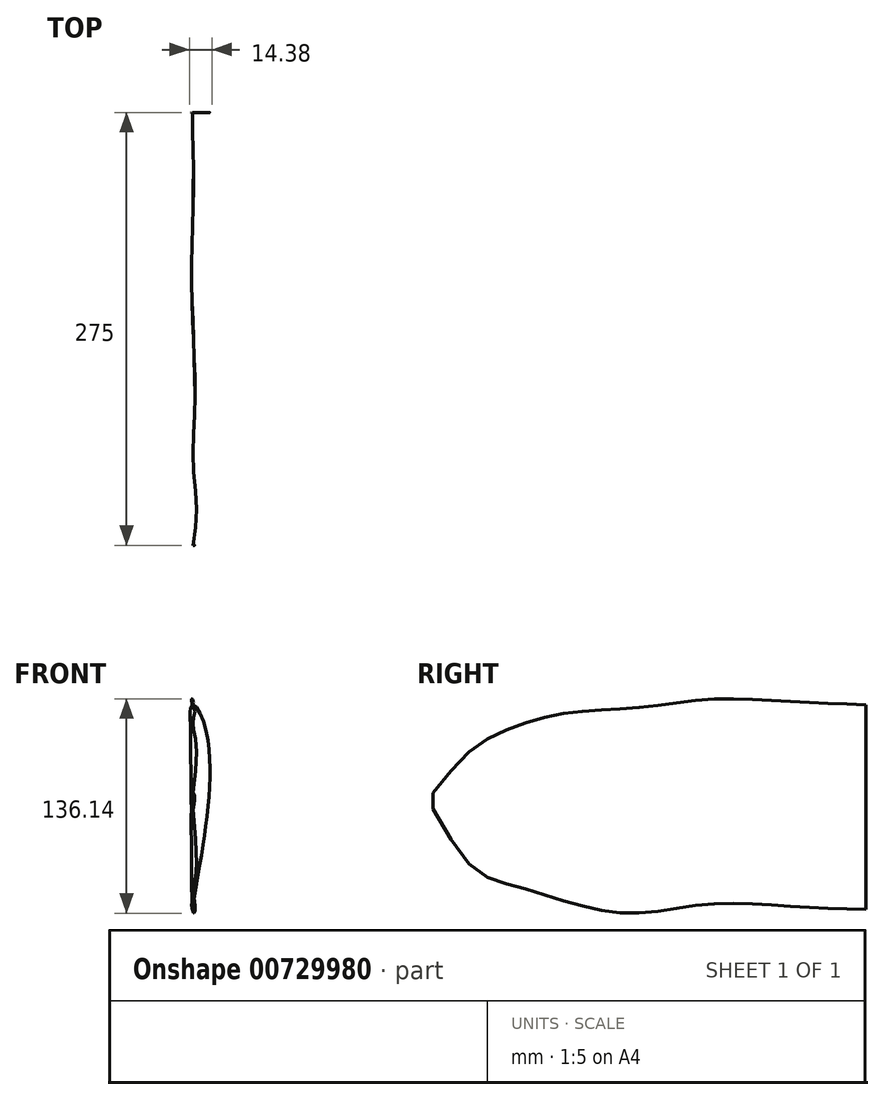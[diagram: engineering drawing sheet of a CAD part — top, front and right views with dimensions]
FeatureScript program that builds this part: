
annotation { "Feature Type Name" : "Feature", "Feature Type Description" : "" }
export const myFeature = defineFeature(function(context is Context, id is Id, definition is map)
    precondition{}
    {
        {
            var Q0;
            Q0=qCreatedBy(makeId("Front.planeOp"),FACE);
            var sketch = newSketch(context, id + "F0", { "sketchPlane" : qUnion([Q0])});
            skFitSpline(sketch, "E0", {"points": [v(-0.6, 60.6) * mm, v(1, 59.9) * mm, v(2.6, 58.2) * mm, v(5, 54) * mm, v(7.3, 47.68) * mm, v(9.21, 39.37) * mm, v(10.11, 32.86) * mm, v(10.51, 25.45) * mm, v(10.61, 18.53) * mm, v(10.51, 11.72) * mm, v(10.11, 3.4) * mm, v(9.51, -3.7) * mm, v(8.4, -12.72) * mm, v(7.5, -20.14) * mm, v(6.55, -27.22) * mm, v(5, -36.27) * mm, v(3.57, -44.14) * mm, v(2.38, -51.16) * mm, v(1.31, -58.43) * mm, v(0.24, -64.75) * mm, v(-0.6, -69.4) * mm], "startDerivative": vector(64.1, -21.66) * mm, "endDerivative": vector(-18.95, -105.25) * mm});
            skFitSpline(sketch, "E1", {"points": [v(-0.6, 60.6) * mm, v(-1.58, 60.1) * mm, v(-1.78, 59.05) * mm, v(-1.93, 58.05) * mm, v(-1.93, 55.8) * mm, v(-1.93, 52.8) * mm, v(-1.83, 48.73) * mm, v(-1.73, 46.83) * mm, v(-1.73, 43.73) * mm, v(-1.73, 40.17) * mm, v(-1.73, 37.41) * mm, v(-1.59, 31.92) * mm, v(-1.59, 28) * mm, v(-1.53, 20.9) * mm, v(-1.47, 11.61) * mm, v(-1.47, 4.1) * mm, v(-1.26, -4.02) * mm, v(-1.26, -8.06) * mm, v(-1.26, -17.16) * mm, v(-1.18, -30.26) * mm, v(-1.16, -34.22) * mm, v(-0.97, -44.95) * mm, v(-0.93, -58.54) * mm, v(-0.6, -69.4) * mm], "startDerivative": vector(-58.23, -16.82) * mm, "endDerivative": vector(6.63, -165.01) * mm});
            skSolve(sketch);
        }
        {
            var Q0;
            Q0=qCreatedBy(makeId("Front.planeOp"),FACE);
            cPlane(context, id + "F1", {"entities" : qUnion([Q0]), "cplaneType" : CPlaneType.OFFSET, "offset" : 275 * mm, "width" : 150 * mm, "height" : 150 * mm});
        }
        {
            var Q0;
            Q0=qCreatedBy(id+"F1.planeOp",FACE);
            var sketch = newSketch(context, id + "F2", { "sketchPlane" : qUnion([Q0])});
            skFitSpline(sketch, "E2", {"points": [v(0, 4.66) * mm, v(0.12, 4.6) * mm, v(0.25, 4.47) * mm, v(0.43, 4.15) * mm, v(0.6, 3.66) * mm, v(0.75, 3.02) * mm, v(0.82, 2.52) * mm, v(0.85, 1.95) * mm, v(0.86, 1.42) * mm, v(0.85, 0.9) * mm, v(0.82, 0.26) * mm, v(0.78, -0.3) * mm, v(0.7, -0.98) * mm, v(0.62, -1.55) * mm, v(0.55, -2.1) * mm, v(0.43, -2.8) * mm, v(0.32, -3.4) * mm, v(0.23, -3.94) * mm, v(0.15, -4.5) * mm, v(0.06, -4.99) * mm, v(0, -5.34) * mm], "startDerivative": vector(4.93, -1.67) * mm, "endDerivative": vector(-1.46, -8.1) * mm});
            skFitSpline(sketch, "E3", {"points": [v(0, 4.66) * mm, v(-0.08, 4.62) * mm, v(-0.1, 4.54) * mm, v(-0.1, 4.46) * mm, v(-0.1, 4.29) * mm, v(-0.1, 4.06) * mm, v(-0.1, 3.74) * mm, v(-0.09, 3.6) * mm, v(-0.09, 3.36) * mm, v(-0.09, 3.08) * mm, v(-0.09, 2.87) * mm, v(-0.08, 2.45) * mm, v(-0.08, 2.15) * mm, v(-0.07, 1.6) * mm, v(-0.07, 0.89) * mm, v(-0.07, 0.31) * mm, v(-0.05, -0.31) * mm, v(-0.05, -0.63) * mm, v(-0.05, -1.33) * mm, v(-0.04, -2.33) * mm, v(-0.04, -2.64) * mm, v(-0.03, -3.46) * mm, v(-0.03, -4.5) * mm, v(0, -5.34) * mm], "startDerivative": vector(-4.48, -1.3) * mm, "endDerivative": vector(0.5, -12.7) * mm});
            skSolve(sketch);
        }
        {
            var Q0;
            Q0=qCreatedBy(makeId("Front.planeOp"),FACE);
            cPlane(context, id + "F3", {"entities" : qUnion([Q0]), "cplaneType" : CPlaneType.OFFSET, "offset" : 250 * mm, "width" : 150 * mm, "height" : 150 * mm});
        }
        {
            var Q0;
            Q0=qCreatedBy(id+"F3.planeOp",FACE);
            var sketch = newSketch(context, id + "F4", { "sketchPlane" : qUnion([Q0])});
            skFitSpline(sketch, "E4", {"points": [v(2.07, 32.54) * mm, v(3, 32.13) * mm, v(3.92, 31.15) * mm, v(5.3, 28.72) * mm, v(6.64, 25.08) * mm, v(7.73, 20.29) * mm, v(8.25, 16.53) * mm, v(8.49, 12.25) * mm, v(8.54, 8.27) * mm, v(8.49, 4.34) * mm, v(8.25, -0.46) * mm, v(7.9, -4.57) * mm, v(7.27, -9.77) * mm, v(6.75, -14.04) * mm, v(6.2, -18.13) * mm, v(5.3, -23.35) * mm, v(4.48, -27.9) * mm, v(3.8, -31.95) * mm, v(3.18, -36.14) * mm, v(2.56, -39.78) * mm, v(2.08, -42.46) * mm], "startDerivative": vector(36.99, -12.5) * mm, "endDerivative": vector(-10.93, -60.72) * mm});
            skFitSpline(sketch, "E5", {"points": [v(2.07, 32.54) * mm, v(1.5, 32.25) * mm, v(1.4, 31.64) * mm, v(1.3, 31.06) * mm, v(1.3, 29.76) * mm, v(1.3, 28.03) * mm, v(1.36, 25.69) * mm, v(1.42, 24.6) * mm, v(1.42, 22.8) * mm, v(1.42, 20.75) * mm, v(1.42, 19.16) * mm, v(1.5, 15.99) * mm, v(1.5, 13.72) * mm, v(1.54, 9.63) * mm, v(1.57, 4.27) * mm, v(1.57, -0.06) * mm, v(1.7, -4.75) * mm, v(1.7, -7.08) * mm, v(1.7, -12.33) * mm, v(1.74, -19.88) * mm, v(1.75, -22.17) * mm, v(1.86, -28.36) * mm, v(1.88, -36.2) * mm, v(2.08, -42.46) * mm], "startDerivative": vector(-33.6, -9.7) * mm, "endDerivative": vector(3.82, -95.2) * mm});
            skSolve(sketch);
        }
        {
            var Q0;
            Q0=qCreatedBy(makeId("Front.planeOp"),FACE);
            cPlane(context, id + "F5", {"entities" : qUnion([Q0]), "cplaneType" : CPlaneType.OFFSET, "offset" : 225 * mm, "width" : 150 * mm, "height" : 150 * mm});
        }
        {
            var Q0;
            Q0=qCreatedBy(id+"F5.planeOp",FACE);
            var sketch = newSketch(context, id + "F6", { "sketchPlane" : qUnion([Q0])});
            skFitSpline(sketch, "E6", {"points": [v(0, 46.1) * mm, v(1.22, 45.55) * mm, v(2.46, 44.24) * mm, v(4.3, 41) * mm, v(6.08, 36.15) * mm, v(7.54, 29.75) * mm, v(8.24, 24.75) * mm, v(8.55, 19.04) * mm, v(8.62, 13.73) * mm, v(8.55, 8.49) * mm, v(8.24, 2.1) * mm, v(7.77, -3.38) * mm, v(6.93, -10.32) * mm, v(6.23, -16.02) * mm, v(5.5, -21.47) * mm, v(4.3, -28.43) * mm, v(3.2, -34.48) * mm, v(2.3, -39.89) * mm, v(1.47, -45.48) * mm, v(0.64, -50.33) * mm, v(0, -53.9) * mm], "startDerivative": vector(49.31, -16.66) * mm, "endDerivative": vector(-14.58, -80.96) * mm});
            skFitSpline(sketch, "E7", {"points": [v(0, 46.1) * mm, v(-0.76, 45.7) * mm, v(-0.91, 44.9) * mm, v(-1.03, 44.13) * mm, v(-1.03, 42.4) * mm, v(-1.03, 40.08) * mm, v(-0.95, 36.96) * mm, v(-0.87, 35.5) * mm, v(-0.87, 33.1) * mm, v(-0.87, 30.37) * mm, v(-0.87, 28.25) * mm, v(-0.76, 24.03) * mm, v(-0.76, 21) * mm, v(-0.72, 15.55) * mm, v(-0.67, 8.4) * mm, v(-0.67, 2.63) * mm, v(-0.51, -3.62) * mm, v(-0.51, -6.73) * mm, v(-0.51, -13.73) * mm, v(-0.45, -23.8) * mm, v(-0.43, -26.85) * mm, v(-0.29, -35.1) * mm, v(-0.26, -45.56) * mm, v(0, -53.9) * mm], "startDerivative": vector(-44.8, -12.94) * mm, "endDerivative": vector(5.1, -126.93) * mm});
            skSolve(sketch);
        }
        {
            var Q0;
            Q0=qCreatedBy(makeId("Front.planeOp"),FACE);
            cPlane(context, id + "F7", {"entities" : qUnion([Q0]), "cplaneType" : CPlaneType.OFFSET, "offset" : 190 * mm, "width" : 150 * mm, "height" : 150 * mm});
        }
        {
            var Q0;
            Q0=qCreatedBy(id+"F7.planeOp",FACE);
            var sketch = newSketch(context, id + "F8", { "sketchPlane" : qUnion([Q0])});
            skFitSpline(sketch, "E8", {"points": [v(0.85, 55.55) * mm, v(2.33, 54.9) * mm, v(3.81, 53.33) * mm, v(6.03, 49.44) * mm, v(8.16, 43.62) * mm, v(9.92, 35.94) * mm, v(10.75, 29.93) * mm, v(11.12, 23.09) * mm, v(11.21, 16.7) * mm, v(11.12, 10.42) * mm, v(10.75, 2.75) * mm, v(10.2, -3.82) * mm, v(9.18, -12.14) * mm, v(8.35, -18.99) * mm, v(7.46, -25.52) * mm, v(6.03, -33.88) * mm, v(4.71, -41.14) * mm, v(3.61, -47.63) * mm, v(2.62, -54.34) * mm, v(1.63, -60.16) * mm, v(0.86, -64.45) * mm], "startDerivative": vector(59.18, -20) * mm, "endDerivative": vector(-17.5, -97.15) * mm});
            skFitSpline(sketch, "E9", {"points": [v(0.85, 55.55) * mm, v(-0.05, 55.08) * mm, v(-0.23, 54.11) * mm, v(-0.37, 53.19) * mm, v(-0.37, 51.1) * mm, v(-0.37, 48.33) * mm, v(-0.28, 44.59) * mm, v(-0.18, 42.83) * mm, v(-0.18, 39.96) * mm, v(-0.18, 36.68) * mm, v(-0.18, 34.14) * mm, v(-0.05, 29.07) * mm, v(-0.05, 25.44) * mm, v(0, 18.9) * mm, v(0.06, 10.32) * mm, v(0.06, 3.4) * mm, v(0.25, -4.1) * mm, v(0.25, -7.84) * mm, v(0.25, -16.24) * mm, v(0.33, -28.33) * mm, v(0.35, -31.99) * mm, v(0.52, -41.9) * mm, v(0.56, -54.44) * mm, v(0.86, -64.45) * mm], "startDerivative": vector(-53.75, -15.52) * mm, "endDerivative": vector(6.12, -152.32) * mm});
            skSolve(sketch);
        }
        {
            var Q0;
            Q0=qCreatedBy(makeId("Front.planeOp"),FACE);
            cPlane(context, id + "F9", {"entities" : qUnion([Q0]), "cplaneType" : CPlaneType.OFFSET, "offset" : 50 * mm, "width" : 150 * mm, "height" : 150 * mm});
        }
        {
            var Q0;
            Q0=qCreatedBy(id+"F9.planeOp",FACE);
            var sketch = newSketch(context, id + "F10", { "sketchPlane" : qUnion([Q0])});
            skFitSpline(sketch, "E10", {"points": [v(-0.01, 62.92) * mm, v(1.6, 62.22) * mm, v(3.2, 60.52) * mm, v(5.6, 56.3) * mm, v(7.9, 50) * mm, v(9.8, 41.68) * mm, v(10.7, 35.17) * mm, v(11.1, 27.76) * mm, v(11.2, 20.85) * mm, v(11.1, 14.03) * mm, v(10.7, 5.72) * mm, v(10.1, -1.4) * mm, v(9, -10.4) * mm, v(8.1, -17.82) * mm, v(7.15, -24.9) * mm, v(5.6, -33.96) * mm, v(4.17, -41.82) * mm, v(2.98, -48.85) * mm, v(1.9, -56.12) * mm, v(0.83, -62.43) * mm, v(0, -67.08) * mm], "startDerivative": vector(64.1, -21.66) * mm, "endDerivative": vector(-18.95, -105.25) * mm});
            skFitSpline(sketch, "E11", {"points": [v(-0.01, 62.92) * mm, v(-0.99, 62.42) * mm, v(-1.19, 61.37) * mm, v(-1.34, 60.36) * mm, v(-1.34, 58.11) * mm, v(-1.34, 55.1) * mm, v(-1.24, 51.05) * mm, v(-1.14, 49.14) * mm, v(-1.14, 46.04) * mm, v(-1.14, 42.48) * mm, v(-1.14, 39.73) * mm, v(-1, 34.24) * mm, v(-1, 30.3) * mm, v(-0.93, 23.22) * mm, v(-0.87, 13.92) * mm, v(-0.87, 6.42) * mm, v(-0.67, -1.7) * mm, v(-0.67, -5.75) * mm, v(-0.67, -14.85) * mm, v(-0.58, -27.95) * mm, v(-0.56, -31.9) * mm, v(-0.38, -42.64) * mm, v(-0.33, -56.23) * mm, v(0, -67.08) * mm], "startDerivative": vector(-58.23, -16.82) * mm, "endDerivative": vector(6.63, -165.01) * mm});
            skSolve(sketch);
        }
        {
            var Q0;
            Q0=qCreatedBy(makeId("Front.planeOp"),FACE);
            cPlane(context, id + "F11", {"entities" : qUnion([Q0]), "cplaneType" : CPlaneType.OFFSET, "offset" : 100 * mm, "width" : 150 * mm, "height" : 150 * mm});
        }
        {
            var Q0;
            Q0=qCreatedBy(id+"F11.planeOp",FACE);
            var sketch = newSketch(context, id + "F12", { "sketchPlane" : qUnion([Q0])});
            skFitSpline(sketch, "E12", {"points": [v(-1.06, 64.1) * mm, v(0.54, 63.4) * mm, v(2.14, 61.7) * mm, v(4.55, 57.48) * mm, v(6.85, 51.17) * mm, v(8.75, 42.86) * mm, v(9.66, 36.35) * mm, v(10.06, 28.93) * mm, v(10.16, 22.02) * mm, v(10.06, 15.2) * mm, v(9.66, 6.9) * mm, v(9.05, -0.22) * mm, v(7.95, -9.23) * mm, v(7.05, -16.65) * mm, v(6.1, -23.73) * mm, v(4.55, -32.78) * mm, v(3.12, -40.65) * mm, v(1.93, -47.68) * mm, v(0.85, -54.94) * mm, v(-0.22, -61.26) * mm, v(-1.05, -65.9) * mm], "startDerivative": vector(64.1, -21.66) * mm, "endDerivative": vector(-18.95, -105.25) * mm});
            skFitSpline(sketch, "E13", {"points": [v(-1.06, 64.1) * mm, v(-2.04, 63.6) * mm, v(-2.24, 62.54) * mm, v(-2.4, 61.54) * mm, v(-2.4, 59.29) * mm, v(-2.4, 56.28) * mm, v(-2.3, 52.22) * mm, v(-2.2, 50.32) * mm, v(-2.2, 47.21) * mm, v(-2.2, 43.66) * mm, v(-2.2, 40.9) * mm, v(-2.04, 35.41) * mm, v(-2.04, 31.48) * mm, v(-1.98, 24.4) * mm, v(-1.92, 15.1) * mm, v(-1.92, 7.6) * mm, v(-1.72, -0.53) * mm, v(-1.72, -4.57) * mm, v(-1.72, -13.67) * mm, v(-1.63, -26.77) * mm, v(-1.61, -30.73) * mm, v(-1.43, -41.46) * mm, v(-1.39, -55.05) * mm, v(-1.05, -65.9) * mm], "startDerivative": vector(-58.23, -16.82) * mm, "endDerivative": vector(6.63, -165.01) * mm});
            skSolve(sketch);
        }
        {
            var Q0;
            Q0=qCreatedBy(makeId("Front.planeOp"),FACE);
            cPlane(context, id + "F13", {"entities" : qUnion([Q0]), "cplaneType" : CPlaneType.OFFSET, "offset" : 150 * mm, "width" : 150 * mm, "height" : 150 * mm});
        }
        {
            var Q0;
            Q0=qCreatedBy(id+"F13.planeOp",FACE);
            var sketch = newSketch(context, id + "F14", { "sketchPlane" : qUnion([Q0])});
            skFitSpline(sketch, "E14", {"points": [v(0.42, 58.35) * mm, v(2.02, 57.65) * mm, v(3.63, 55.95) * mm, v(6.03, 51.74) * mm, v(8.34, 45.43) * mm, v(10.24, 37.12) * mm, v(11.14, 30.6) * mm, v(11.54, 23.2) * mm, v(11.64, 16.28) * mm, v(11.54, 9.47) * mm, v(11.14, 1.15) * mm, v(10.54, -5.96) * mm, v(9.44, -14.98) * mm, v(8.54, -22.4) * mm, v(7.58, -29.47) * mm, v(6.03, -38.53) * mm, v(4.6, -46.4) * mm, v(3.41, -53.42) * mm, v(2.34, -60.69) * mm, v(1.27, -67) * mm, v(0.43, -71.65) * mm], "startDerivative": vector(64.1, -21.66) * mm, "endDerivative": vector(-18.95, -105.25) * mm});
            skFitSpline(sketch, "E15", {"points": [v(0.42, 58.35) * mm, v(-0.55, 57.85) * mm, v(-0.76, 56.8) * mm, v(-0.9, 55.8) * mm, v(-0.9, 53.54) * mm, v(-0.9, 50.54) * mm, v(-0.8, 46.48) * mm, v(-0.7, 44.58) * mm, v(-0.7, 41.47) * mm, v(-0.7, 37.91) * mm, v(-0.7, 35.16) * mm, v(-0.56, 29.67) * mm, v(-0.56, 25.74) * mm, v(-0.5, 18.65) * mm, v(-0.44, 9.36) * mm, v(-0.44, 1.85) * mm, v(-0.23, -6.27) * mm, v(-0.23, -10.32) * mm, v(-0.23, -19.41) * mm, v(-0.15, -32.51) * mm, v(-0.13, -36.47) * mm, v(0.06, -47.2) * mm, v(0.1, -60.8) * mm, v(0.43, -71.65) * mm], "startDerivative": vector(-58.23, -16.82) * mm, "endDerivative": vector(6.63, -165.01) * mm});
            skSolve(sketch);
        }
        {
            var Q0;
            Q0=makeQuery(id+"F0.imprint","IMPRINT",FACE,{"disambiguationData":[TD([[makeQuery(id+"F0.imprint","IMPRINT",EDGE,{"derivedFrom":sQuery(id+"F0.wireOp",EDGE,"E0")}),-1.0]])]});
            var Q1;
            Q1=makeQuery(id+"F10.imprint","IMPRINT",FACE,{"disambiguationData":[TD([[makeQuery(id+"F10.imprint","IMPRINT",EDGE,{"derivedFrom":sQuery(id+"F10.wireOp",EDGE,"E10")}),-1.0]])]});
            var Q2;
            Q2=makeQuery(id+"F12.imprint","IMPRINT",FACE,{"disambiguationData":[TD([[makeQuery(id+"F12.imprint","IMPRINT",EDGE,{"derivedFrom":sQuery(id+"F12.wireOp",EDGE,"E12")}),-1.0]])]});
            var Q3;
            Q3=makeQuery(id+"F14.imprint","IMPRINT",FACE,{"disambiguationData":[TD([[makeQuery(id+"F14.imprint","IMPRINT",EDGE,{"derivedFrom":sQuery(id+"F14.wireOp",EDGE,"E14")}),-1.0]])]});
            var Q4;
            Q4=makeQuery(id+"F8.imprint","IMPRINT",FACE,{"disambiguationData":[TD([[makeQuery(id+"F8.imprint","IMPRINT",EDGE,{"derivedFrom":sQuery(id+"F8.wireOp",EDGE,"E8")}),-1.0]])]});
            var Q5;
            Q5=makeQuery(id+"F6.imprint","IMPRINT",FACE,{"disambiguationData":[TD([[makeQuery(id+"F6.imprint","IMPRINT",EDGE,{"derivedFrom":sQuery(id+"F6.wireOp",EDGE,"E6")}),-1.0]])]});
            var Q6;
            Q6=makeQuery(id+"F4.imprint","IMPRINT",FACE,{"disambiguationData":[TD([[makeQuery(id+"F4.imprint","IMPRINT",EDGE,{"derivedFrom":sQuery(id+"F4.wireOp",EDGE,"E4")}),-1.0]])]});
            var Q7;
            Q7=makeQuery(id+"F2.imprint","IMPRINT",FACE,{"disambiguationData":[TD([[makeQuery(id+"F2.imprint","IMPRINT",EDGE,{"derivedFrom":sQuery(id+"F2.wireOp",EDGE,"E2")}),-1.0]])]});
            loft(context, id + "F15", {"sheetProfilesArray" : [{ "sheetProfileEntities" : qUnion([Q0]) }, { "sheetProfileEntities" : qUnion([Q1]) }, { "sheetProfileEntities" : qUnion([Q2]) }, { "sheetProfileEntities" : qUnion([Q3]) }, { "sheetProfileEntities" : qUnion([Q4]) }, { "sheetProfileEntities" : qUnion([Q5]) }, { "sheetProfileEntities" : qUnion([Q6]) }, { "sheetProfileEntities" : qUnion([Q7]) }]});
        }
    });
